annotation { "Feature Type Name" : "Feature", "Feature Type Description" : "" }
export const myFeature = defineFeature(function(context is Context, id is Id, definition is map)
    precondition{}
    {
        {
            var Q0;
            Q0=qCreatedBy(makeId("Top.planeOp"),FACE);
            var sketch = newSketch(context, id + "F0", { "sketchPlane" : qUnion([Q0])});
            skLineSegment(sketch, "E0.bottom", {"start": v(-88.9, 74.93) * mm, "end": v(88.9, 74.93) * mm});
            skLineSegment(sketch, "E0.top", {"start": v(-88.9, -74.93) * mm, "end": v(88.9, -74.93) * mm});
            skLineSegment(sketch, "E0.left", {"start": v(-88.9, 74.93) * mm, "end": v(-88.9, -74.93) * mm});
            skLineSegment(sketch, "E0.right", {"start": v(88.9, 74.93) * mm, "end": v(88.9, -74.93) * mm});
            skLineSegment(sketch, "E1", {"start": v(0, 74.93) * mm, "end": v(0, -74.93) * mm, "construction": true});
            skLineSegment(sketch, "E2", {"start": v(-88.9, 0) * mm, "end": v(88.9, 0) * mm, "construction": true});
            skSolve(sketch);
        }
        {
            var Q0;
            Q0=makeQuery(id+"F0.imprint","IMPRINT",FACE,{"disambiguationData":[TD([[makeQuery(id+"F0.imprint","IMPRINT",EDGE,{"derivedFrom":sQuery(id+"F0.wireOp",EDGE,"E0.bottom")}),-1.0]])]});
            extrude(context, id + "F1", {"entities" : qUnion([Q0]), "depth" : 19.05 * mm, "offsetDistance" : 25.4 * mm});
        }
        {
            var Q0;
            Q0=makeQuery(id+"F1.opExtrude","CAP_FACE",FACE,{"disambiguationData":[OSD([sQuery(id+"F0.wireOp",EDGE,"E0.bottom"),sQuery(id+"F0.wireOp",EDGE,"E0.top"),sQuery(id+"F0.wireOp",EDGE,"E0.left"),sQuery(id+"F0.wireOp",EDGE,"E0.right")])],"isStart":false});
            var sketch = newSketch(context, id + "F2", { "sketchPlane" : qUnion([Q0])});
            skLineSegment(sketch, "E3", {"start": v(-88.9, -65.4) * mm, "end": v(88.9, -65.4) * mm, "construction": true});
            skPoint(sketch, "E4", {"position": v(-68.58, -65.4) * mm});
            skPoint(sketch, "E5.1.0.0", {"position": v(-48.26, -65.4) * mm});
            skPoint(sketch, "E5.2.0.0", {"position": v(-27.94, -65.4) * mm});
            skPoint(sketch, "E5.3.0.0", {"position": v(-7.62, -65.4) * mm});
            skLineSegment(sketch, "E5.direction1", {"start": v(-68.58, -65.4) * mm, "end": v(-48.26, -65.4) * mm, "construction": true});
            skLineSegment(sketch, "E6", {"start": v(-68.58, 74.93) * mm, "end": v(-68.58, -74.93) * mm, "construction": true});
            skPoint(sketch, "E7", {"position": v(-68.58, 65.4) * mm});
            skLineSegment(sketch, "E8.direction1", {"start": v(-68.58, 65.4) * mm, "end": v(-48.26, 65.4) * mm, "construction": true});
            skLineSegment(sketch, "E8.direction2", {"start": v(-68.58, 65.4) * mm, "end": v(-68.58, 53.98) * mm, "construction": true});
            skLineSegment(sketch, "E9", {"start": v(-88.9, -22.48) * mm, "end": v(88.9, -22.48) * mm, "construction": true});
            skPoint(sketch, "E10", {"position": v(-38.1, -22.48) * mm});
            skPoint(sketch, "E11.0.1.0", {"position": v(-38.1, 22.48) * mm});
            skPoint(sketch, "E11.1.0.0", {"position": v(49.85, -22.47) * mm});
            skPoint(sketch, "E11.1.1.0", {"position": v(49.85, 22.48) * mm});
            skLineSegment(sketch, "E11.direction1", {"start": v(-38.1, -22.48) * mm, "end": v(49.85, -22.48) * mm, "construction": true});
            skLineSegment(sketch, "E11.direction2", {"start": v(-38.1, -22.48) * mm, "end": v(-38.1, 22.48) * mm, "construction": true});
            skPoint(sketch, "E12.0.1.0", {"position": v(-48.26, 65.4) * mm});
            skPoint(sketch, "E12.0.2.0", {"position": v(-27.94, 65.4) * mm});
            skPoint(sketch, "E12.0.3.0", {"position": v(-7.62, 65.4) * mm});
            skSolve(sketch);
        }
        {
            var Q0;
            Q0=makeQuery(id+"F1.opExtrude","SWEPT_FACE",FACE,{"disambiguationData":[OSD([sQuery(id+"F0.wireOp",EDGE,"E0.top")])]});
            var sketch = newSketch(context, id + "F3", { "sketchPlane" : qUnion([Q0])});
            skLineSegment(sketch, "E13", {"start": v(-88.9, 9.53) * mm, "end": v(88.9, 9.53) * mm, "construction": true});
            skPoint(sketch, "E14", {"position": v(-68.58, 9.52) * mm});
            skPoint(sketch, "E15.1.0.0", {"position": v(-48.26, 9.52) * mm});
            skPoint(sketch, "E15.2.0.0", {"position": v(-27.94, 9.52) * mm});
            skPoint(sketch, "E15.3.0.0", {"position": v(-7.62, 9.52) * mm});
            skLineSegment(sketch, "E15.direction1", {"start": v(-68.58, 9.53) * mm, "end": v(-48.26, 9.53) * mm, "construction": true});
            skSolve(sketch);
        }
        {
            var Q0;
            Q0=makeQuery(id+"F1.opExtrude","SWEPT_FACE",FACE,{"disambiguationData":[OSD([sQuery(id+"F0.wireOp",EDGE,"E0.bottom")])]});
            var sketch = newSketch(context, id + "F4", { "sketchPlane" : qUnion([Q0])});
            skLineSegment(sketch, "E16", {"start": v(-88.9, 9.53) * mm, "end": v(88.9, 9.53) * mm, "construction": true});
            skPoint(sketch, "E17", {"position": v(7.62, 9.52) * mm});
            skPoint(sketch, "E18.1.0.0", {"position": v(27.94, 9.52) * mm});
            skPoint(sketch, "E18.2.0.0", {"position": v(48.26, 9.52) * mm});
            skPoint(sketch, "E18.3.0.0", {"position": v(68.58, 9.52) * mm});
            skLineSegment(sketch, "E18.direction1", {"start": v(7.62, 9.53) * mm, "end": v(27.94, 9.53) * mm, "construction": true});
            skSolve(sketch);
        }
        {
            var Q0;
            Q0=sQuery(id+"F2.wireOp",VERTEX,"E4");
            var Q1;
            Q1=sQuery(id+"F2.wireOp",VERTEX,"E5.1.0.0");
            var Q2;
            Q2=sQuery(id+"F2.wireOp",VERTEX,"E5.2.0.0");
            var Q3;
            Q3=sQuery(id+"F2.wireOp",VERTEX,"E5.3.0.0");
            var Q4;
            Q4=sQuery(id+"F2.wireOp",VERTEX,"E12.0.3.0");
            var Q5;
            Q5=sQuery(id+"F2.wireOp",VERTEX,"E12.0.2.0");
            var Q6;
            Q6=sQuery(id+"F2.wireOp",VERTEX,"E12.0.1.0");
            var Q7;
            Q7=sQuery(id+"F2.wireOp",VERTEX,"E7");
            var Q8;
            Q8=makeQuery(id+"F1.opExtrude","SWEPT_BODY",BODY,{"disambiguationData":[OSD([sQuery(id+"F0.wireOp",EDGE,"E0.bottom"),sQuery(id+"F0.wireOp",EDGE,"E0.top"),sQuery(id+"F0.wireOp",EDGE,"E0.left"),sQuery(id+"F0.wireOp",EDGE,"E0.right")])]});
            hole(context, id + "F5", {"style" : HoleStyle.SIMPLE, "endStyle" : HoleEndStyle.BLIND, "standardTappedOrClearance" : lookupTablePath({ "standard" : "ANSI", "size" : "3/8 (0.38)", "type" : "Drilled" }), "standardBlindInLast" : lookupTablePath({ "standard" : "ANSI", "size" : "3/8", "type" : "Drilled" }), "holeDiameter" : 3 / 203.2 * mm, "majorDiameter" : 6.35 * mm, "holeDepth" : 16.54 * mm, "isTappedThrough" : true, "tappedDepth" : 12.7 * mm, "tapClearance" : 3, "startFromSketch" : true, "locations" : qUnion([Q0, Q1, Q2, Q3, Q4, Q5, Q6, Q7]), "scope" : qUnion([Q8])});
        }
        {
            var Q0;
            Q0=sQuery(id+"F3.wireOp",VERTEX,"E15.3.0.0");
            var Q1;
            Q1=sQuery(id+"F3.wireOp",VERTEX,"E15.2.0.0");
            var Q2;
            Q2=sQuery(id+"F3.wireOp",VERTEX,"E15.1.0.0");
            var Q3;
            Q3=sQuery(id+"F3.wireOp",VERTEX,"E14");
            var Q4;
            Q4=sQuery(id+"F4.wireOp",VERTEX,"E18.3.0.0");
            var Q5;
            Q5=sQuery(id+"F4.wireOp",VERTEX,"E18.2.0.0");
            var Q6;
            Q6=sQuery(id+"F4.wireOp",VERTEX,"E18.1.0.0");
            var Q7;
            Q7=sQuery(id+"F4.wireOp",VERTEX,"E17");
            var Q8;
            Q8=makeQuery(id+"F1.opExtrude","SWEPT_BODY",BODY,{"disambiguationData":[OSD([sQuery(id+"F0.wireOp",EDGE,"E0.bottom"),sQuery(id+"F0.wireOp",EDGE,"E0.top"),sQuery(id+"F0.wireOp",EDGE,"E0.left"),sQuery(id+"F0.wireOp",EDGE,"E0.right")])]});
            hole(context, id + "F6", {"style" : HoleStyle.SIMPLE, "endStyle" : HoleEndStyle.BLIND, "standardTappedOrClearance" : lookupTablePath({ "standard" : "ANSI", "fit" : "Normal (ASME)", "size" : "1/4", "type" : "Clearance" }), "standardBlindInLast" : lookupTablePath({ "fit" : "Free", "standard" : "ANSI", "size" : "1/4", "type" : "Clearance" }), "holeDiameter" : 6.76 * mm, "majorDiameter" : 6.35 * mm, "holeDepth" : 16.54 * mm, "isTappedThrough" : true, "tappedDepth" : 12.7 * mm, "tapClearance" : 3, "startFromSketch" : true, "locations" : qUnion([Q0, Q1, Q2, Q3, Q4, Q5, Q6, Q7]), "scope" : qUnion([Q8])});
        }
        {
            var Q0;
            Q0=sQuery(id+"F2.wireOp",VERTEX,"E10");
            var Q1;
            Q1=sQuery(id+"F2.wireOp",VERTEX,"E11.0.1.0");
            var Q2;
            Q2=sQuery(id+"F2.wireOp",VERTEX,"E11.1.1.0");
            var Q3;
            Q3=sQuery(id+"F2.wireOp",VERTEX,"E11.1.0.0");
            var Q4;
            Q4=makeQuery(id+"F1.opExtrude","SWEPT_BODY",BODY,{"disambiguationData":[OSD([sQuery(id+"F0.wireOp",EDGE,"E0.bottom"),sQuery(id+"F0.wireOp",EDGE,"E0.top"),sQuery(id+"F0.wireOp",EDGE,"E0.left"),sQuery(id+"F0.wireOp",EDGE,"E0.right")])]});
            hole(context, id + "F7", {"style" : HoleStyle.SIMPLE, "endStyle" : HoleEndStyle.THROUGH, "standardTappedOrClearance" : lookupTablePath({ "standard" : "ISO", "fit" : "Close", "size" : "M8", "type" : "Clearance" }), "standardBlindInLast" : lookupTablePath({ "fit" : "Close", "standard" : "ISO", "size" : "M8", "type" : "Clearance" }), "holeDiameter" : 8.4 * mm, "majorDiameter" : 6.35 * mm, "isTappedThrough" : true, "tappedDepth" : 12.7 * mm, "tapClearance" : 3, "startFromSketch" : true, "locations" : qUnion([Q0, Q1, Q2, Q3]), "scope" : qUnion([Q4])});
        }
    });